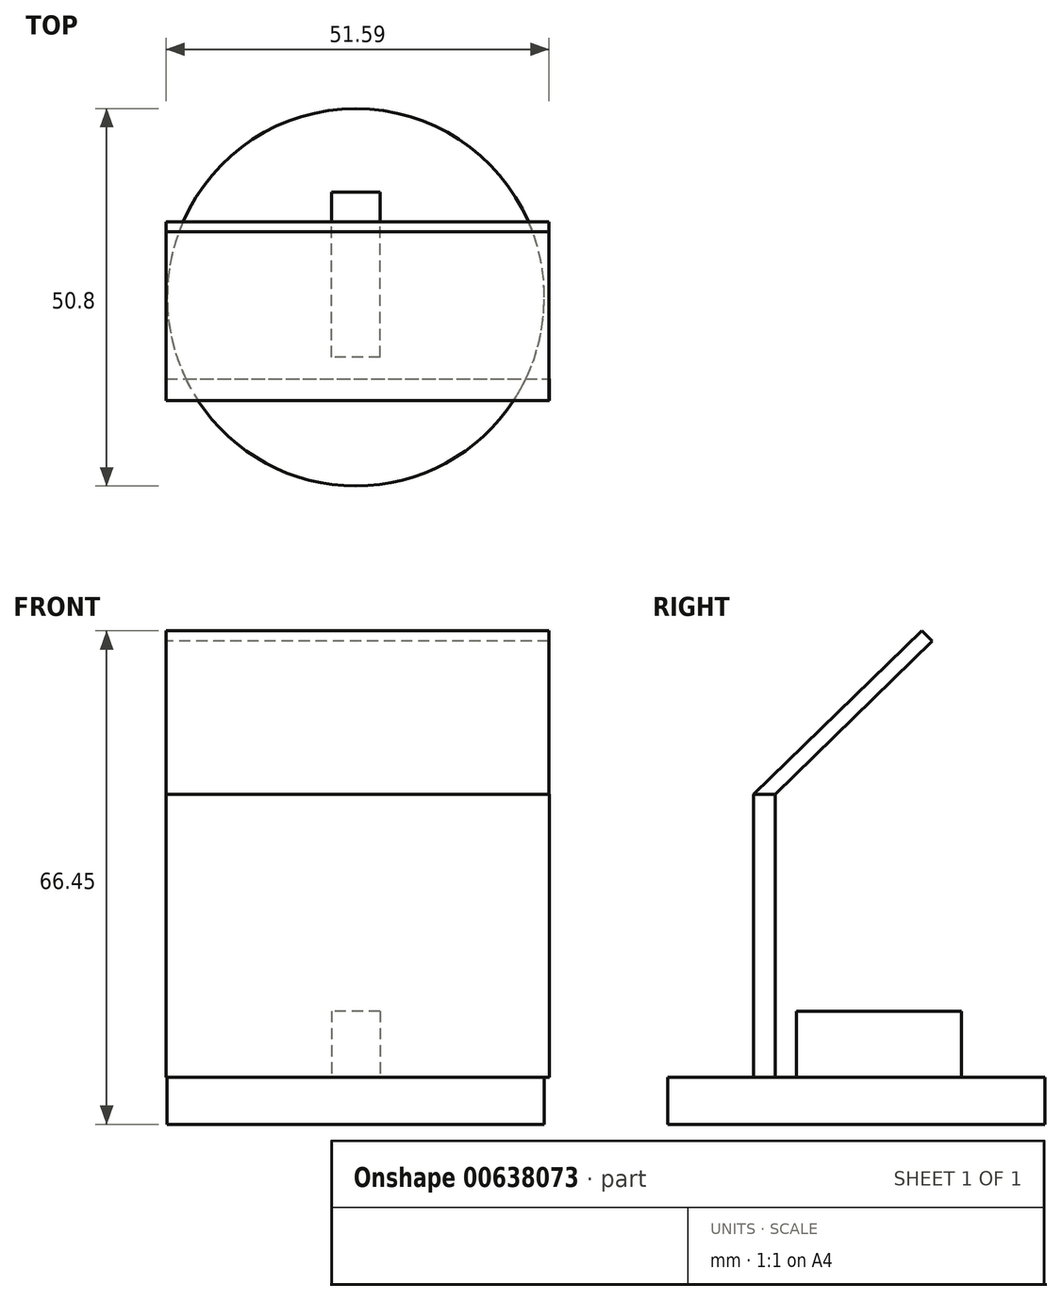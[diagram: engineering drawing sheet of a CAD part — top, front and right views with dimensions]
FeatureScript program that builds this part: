
annotation { "Feature Type Name" : "Feature", "Feature Type Description" : "" }
export const myFeature = defineFeature(function(context is Context, id is Id, definition is map)
    precondition{}
    {
        {
            var Q0;
            Q0=qCreatedBy(makeId("Top.planeOp"),FACE);
            var sketch = newSketch(context, id + "F0", { "sketchPlane" : qUnion([Q0])});
            skCircle(sketch, "E0", {"center": v(0, 0) * mm, "radius": 25.4 * mm});
            skSolve(sketch);
        }
        {
            var Q0;
            Q0 = qSketchRegion(id + "F0", true);
            extrude(context, id + "F1", {"entities" : qUnion([Q0]), "depth" : 6.35 * mm, "offsetDistance" : 25.4 * mm});
        }
        {
            var Q0;
            Q0=makeQuery(id+"F1.opExtrude","CAP_FACE",FACE,{"disambiguationData":[OSD([sQuery(id+"F0.wireOp",EDGE,"E0")])],"isStart":false});
            var sketch = newSketch(context, id + "F2", { "sketchPlane" : qUnion([Q0])});
            skLineSegment(sketch, "E1.bottom", {"start": v(-25.55, -10.97) * mm, "end": v(26.04, -10.97) * mm});
            skLineSegment(sketch, "E1.top", {"start": v(-25.55, -13.88) * mm, "end": v(26.04, -13.88) * mm});
            skLineSegment(sketch, "E1.left", {"start": v(-25.55, -10.97) * mm, "end": v(-25.55, -13.88) * mm});
            skLineSegment(sketch, "E1.right", {"start": v(26.04, -10.97) * mm, "end": v(26.04, -13.88) * mm});
            skSolve(sketch);
        }
        {
            var Q0;
            Q0 = qSketchRegion(id + "F2", true);
            extrude(context, id + "F3", {"entities" : qUnion([Q0]), "operationType" : NewBodyOperationType.ADD, "depth" : 38.1 * mm, "offsetDistance" : 25.4 * mm});
        }
        {
            var Q0;
            Q0=makeQuery(id+"F3.opExtrude","SWEPT_FACE",FACE,{"disambiguationData":[OSD([sQuery(id+"F2.wireOp",EDGE,"E1.left")])]});
            var sketch = newSketch(context, id + "F4", { "sketchPlane" : qUnion([Q0])});
            skLineSegment(sketch, "E2", {"start": v(13.88, 44.45) * mm, "end": v(-8.8, 66.45) * mm});
            skLineSegment(sketch, "E3", {"start": v(-8.8, 66.45) * mm, "end": v(-10.17, 65.03) * mm});
            skLineSegment(sketch, "E4", {"start": v(-10.17, 65.03) * mm, "end": v(10.97, 44.45) * mm});
            skLineSegment(sketch, "E5", {"start": v(10.97, 44.45) * mm, "end": v(13.88, 44.45) * mm});
            skSolve(sketch);
        }
        {
            var Q0;
            Q0 = qSketchRegion(id + "F4", true);
            extrude(context, id + "F5", {"entities" : qUnion([Q0]), "operationType" : NewBodyOperationType.ADD, "oppositeDirection" : true, "depth" : 51.56 * mm, "offsetDistance" : 25.4 * mm});
        }
        {
            var Q0;
            {var subQ0=sQuery(id+"F0.wireOp",EDGE,"E0");var subQ1=sQuery(id+"F2.wireOp",EDGE,"E1.bottom");Q0=makeQuery(id+"F3.boolean.opBoolean","SPLIT",FACE,{"disambiguationData":[TD([makeQuery(id+"F3.opExtrude","SWEPT_FACE",FACE,{"disambiguationData":[OSD([subQ1])]})])],"derivedFrom":makeQuery(id+"F1.opExtrude","CAP_FACE",FACE,{"disambiguationData":[OSD([subQ0])],"isStart":false})});}
            var sketch = newSketch(context, id + "F6", { "sketchPlane" : qUnion([Q0])});
            skLineSegment(sketch, "E6.bottom", {"start": v(3.27, -8.07) * mm, "end": v(-3.28, -8.07) * mm});
            skLineSegment(sketch, "E6.top", {"start": v(3.27, 14.15) * mm, "end": v(-3.28, 14.15) * mm});
            skLineSegment(sketch, "E6.left", {"start": v(3.27, -8.07) * mm, "end": v(3.27, 14.15) * mm});
            skLineSegment(sketch, "E6.right", {"start": v(-3.28, -8.07) * mm, "end": v(-3.28, 14.15) * mm});
            skSolve(sketch);
        }
        {
            var Q0;
            Q0 = qSketchRegion(id + "F6", true);
            extrude(context, id + "F7", {"entities" : qUnion([Q0]), "operationType" : NewBodyOperationType.ADD, "depth" : 8.9 * mm, "offsetDistance" : 25.4 * mm});
        }
    });
